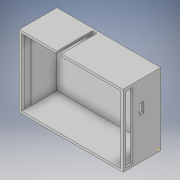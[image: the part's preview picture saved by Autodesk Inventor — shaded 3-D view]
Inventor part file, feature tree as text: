
AUTODESK INVENTOR PART (.ipt)
format: ipt  version: 2018.3 (Build 223284000, 284)  size: 131,072 bytes
history: native  units: in
note: dims shown in document units (in); Inventor stores cm internally (conversion verified against a paired STEP export)
features: sketch x5, extrude x4, shell x1
ambient origin geometry x8: Origin, YZ Plane, XZ Plane, XY Plane, X Axis, Y Axis, Z Axis, Center Point
bodies: Solid1 (feature_tree)
feature tree (10):
  extrude  "Extrusion1"  Depth=2.2441in
  shell  "Shell1"  Thickness=1.1811in
  sketch  "Sketch2"  dims[d4=0.0787in d5=0.236in]
  extrude  "Extrusion2"  Depth=0.236in
  extrude  "Extrusion3"  Depth=3.4252in TaperAngle=0.0deg
  extrude  "Extrusion4"  Depth=0.335in
  sketch  "Sketch1"  dims[d0=3.307in d1=2.2441in d2=1.1811in d3=0.0in]
  sketch  "Sketch3"  dims[d6=2.2047in d7=3.4252in d8=0.0in]
  sketch  "Sketch4"  dims[d9=0.157in d10=0.335in]
  sketch  "Sketch5"  dims[d11=0.5in d12=0.0in d13=0.154in d14=0.5in d15=0.0in]
